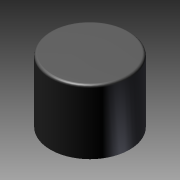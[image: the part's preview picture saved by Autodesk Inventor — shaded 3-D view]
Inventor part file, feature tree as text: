
AUTODESK INVENTOR PART (.ipt)
format: ipt  version: 2014 (Build 180170000, 170)  size: 98,816 bytes
history: native  units: in
note: dims shown in document units (in); Inventor stores cm internally (conversion verified against a paired STEP export)
features: other x14, revolve x1, sketch x1
ambient origin geometry x8: Origin, YZ Plane, XZ Plane, XY Plane, X Axis, Y Axis, Z Axis, Center Point
bodies: Solid1 (feature_tree)
feature tree (16):
  revolve  "Revolution1"  [1 undecoded]
  other  "to_body_XY"
  other  "to_body_YZ"
  other  "to_body_ZX"
  other  "to_body_X"
  other  "to_body_Y"
  other  "to_body_Z"
  other  "to_body_Center"
  other  "to_cap_XY"
  other  "to_cap_YZ"
  other  "to_cap_ZX"
  other  "to_cap_X"
  other  "to_cap_Y"
  other  "to_cap_Z"
  other  "to_cap_Center"
  sketch  "Sketch_2"  dims[d0=360.0deg]
note: 1 required parameter value undecoded (feature->parameter linkage not recoverable at this tier; creation-order binding heuristic only, values carry confidence <= 0.55)
